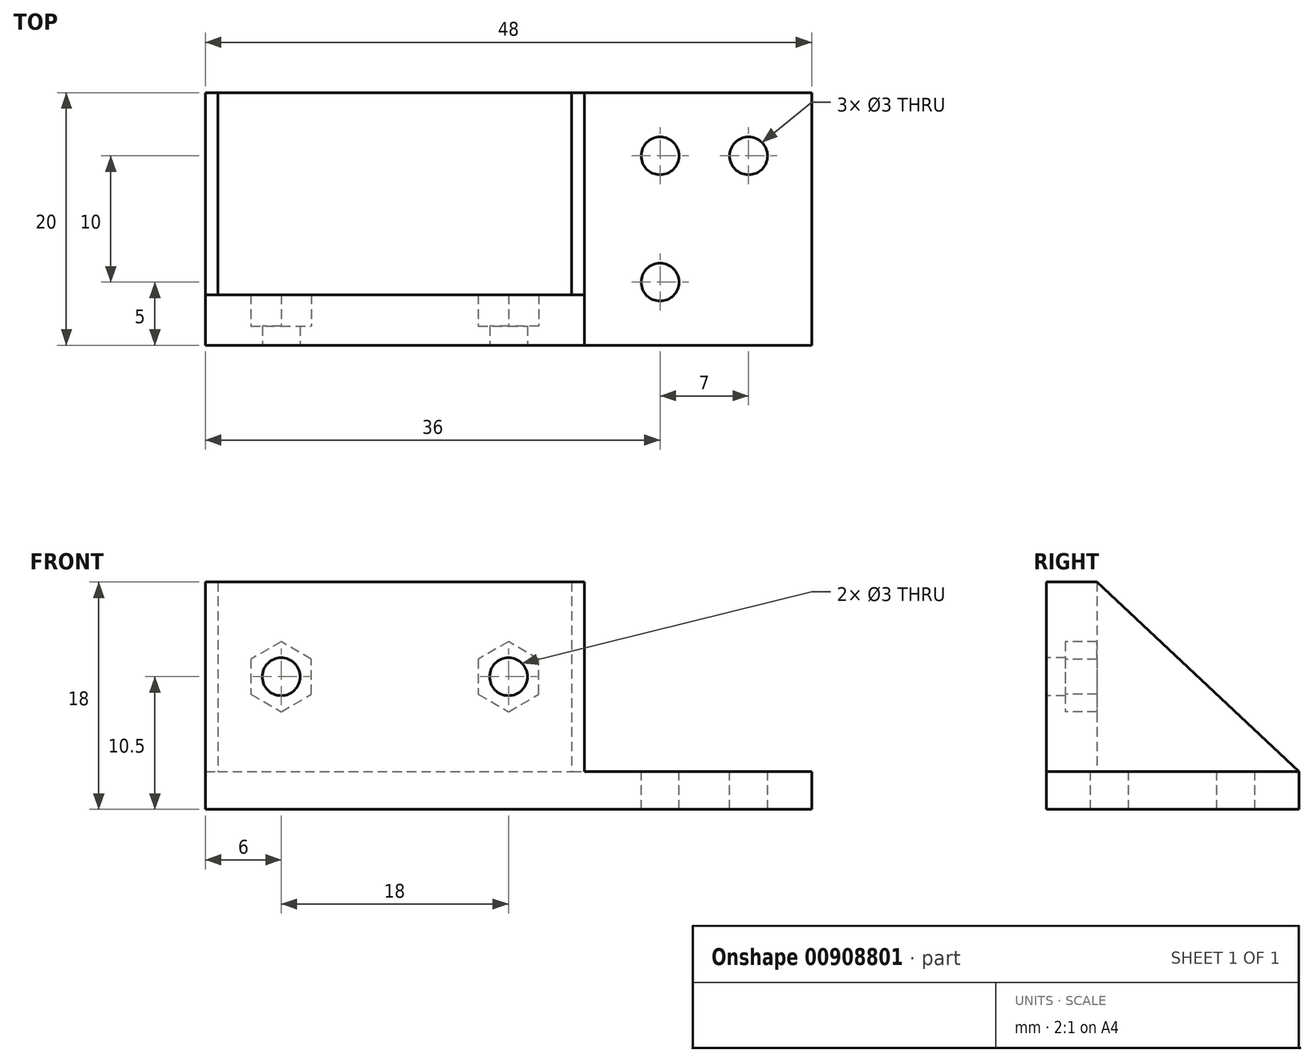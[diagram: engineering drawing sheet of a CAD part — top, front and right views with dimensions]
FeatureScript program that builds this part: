
annotation { "Feature Type Name" : "Feature", "Feature Type Description" : "" }
export const myFeature = defineFeature(function(context is Context, id is Id, definition is map)
    precondition{}
    {
        {
            var Q0;
            Q0=qCreatedBy(makeId("Top.planeOp"),FACE);
            var sketch = newSketch(context, id + "F0", { "sketchPlane" : qUnion([Q0])});
            skLineSegment(sketch, "E0.bottom", {"start": v(-24, 10) * mm, "end": v(24, 10) * mm});
            skLineSegment(sketch, "E0.top", {"start": v(-24, -10) * mm, "end": v(24, -10) * mm});
            skLineSegment(sketch, "E0.left", {"start": v(-24, 10) * mm, "end": v(-24, -10) * mm});
            skLineSegment(sketch, "E0.right", {"start": v(24, 10) * mm, "end": v(24, -10) * mm});
            skSolve(sketch);
        }
        {
            var Q0;
            Q0=makeQuery(id+"F0.imprint","IMPRINT",FACE,{"disambiguationData":[TD([[makeQuery(id+"F0.imprint","IMPRINT",EDGE,{"derivedFrom":sQuery(id+"F0.wireOp",EDGE,"E0.bottom")}),-1.0]])]});
            extrude(context, id + "F1", {"entities" : qUnion([Q0]), "depth" : 3 * mm, "offsetDistance" : 25 * mm});
        }
        {
            var Q0;
            Q0=makeQuery(id+"F1.opExtrude","CAP_FACE",FACE,{"disambiguationData":[OSD([sQuery(id+"F0.wireOp",EDGE,"E0.bottom"),sQuery(id+"F0.wireOp",EDGE,"E0.top"),sQuery(id+"F0.wireOp",EDGE,"E0.left"),sQuery(id+"F0.wireOp",EDGE,"E0.right")])],"isStart":false});
            var sketch = newSketch(context, id + "F2", { "sketchPlane" : qUnion([Q0])});
            skLineSegment(sketch, "E1.bottom", {"start": v(-24, -10) * mm, "end": v(6, -10) * mm});
            skLineSegment(sketch, "E1.top", {"start": v(-24, -8.5) * mm, "end": v(6, -8.5) * mm});
            skLineSegment(sketch, "E1.left", {"start": v(-24, -10) * mm, "end": v(-24, -8.5) * mm});
            skLineSegment(sketch, "E1.right", {"start": v(6, -10) * mm, "end": v(6, -8.5) * mm});
            skSolve(sketch);
        }
        {
            var Q0;
            Q0 = qSketchRegion(id + "F2", true);
            extrude(context, id + "F3", {"entities" : qUnion([Q0]), "operationType" : NewBodyOperationType.ADD, "depth" : 15 * mm, "offsetDistance" : 25 * mm});
        }
        {
            var Q0;
            Q0=makeQuery(id+"F3.boolean.opBoolean","MERGE",FACE,{"derivedFrom":[makeQuery(id+"F1.opExtrude","SWEPT_FACE",FACE,{"disambiguationData":[OSD([sQuery(id+"F0.wireOp",EDGE,"E0.top")])]}),makeQuery(id+"F3.opExtrude","SWEPT_FACE",FACE,{"disambiguationData":[OSD([sQuery(id+"F2.wireOp",EDGE,"E1.bottom")])]})]});
            var sketch = newSketch(context, id + "F4", { "sketchPlane" : qUnion([Q0])});
            skPoint(sketch, "E2", {"position": v(-18, 10.5) * mm});
            skPoint(sketch, "E3", {"position": v(0, 10.5) * mm});
            skLineSegment(sketch, "E4", {"start": v(-9, 16.14) * mm, "end": v(-9, 2.45) * mm, "construction": true});
            skLineSegment(sketch, "E5", {"start": v(6, 3) * mm, "end": v(-24, 3) * mm, "construction": true});
            skLineSegment(sketch, "E6", {"start": v(-18, 3) * mm, "end": v(-18, 18) * mm, "construction": true});
            skSolve(sketch);
        }
        {
            var Q0;
            Q0=makeQuery(id+"F1.opExtrude","CAP_FACE",FACE,{"disambiguationData":[OSD([sQuery(id+"F0.wireOp",EDGE,"E0.bottom"),sQuery(id+"F0.wireOp",EDGE,"E0.top"),sQuery(id+"F0.wireOp",EDGE,"E0.left"),sQuery(id+"F0.wireOp",EDGE,"E0.right")])],"isStart":false});
            var sketch = newSketch(context, id + "F5", { "sketchPlane" : qUnion([Q0])});
            skLineSegment(sketch, "E7", {"start": v(12, -20) * mm, "end": v(12, 10) * mm, "construction": true});
            skPoint(sketch, "E8", {"position": v(12, 5) * mm});
            skPoint(sketch, "E9", {"position": v(12, -5) * mm});
            skPoint(sketch, "E10", {"position": v(19, 5) * mm});
            skSolve(sketch);
        }
        {
            var Q0;
            Q0=sQuery(id+"F4.wireOp",VERTEX,"E3");
            var Q1;
            Q1=sQuery(id+"F4.wireOp",VERTEX,"E2");
            var Q2;
            Q2=sQuery(id+"F5.wireOp",VERTEX,"E10");
            var Q3;
            Q3=sQuery(id+"F5.wireOp",VERTEX,"E8");
            var Q4;
            Q4=sQuery(id+"F5.wireOp",VERTEX,"E9");
            var Q5;
            Q5=makeQuery(id+"F1.opExtrude","SWEPT_BODY",BODY,{"disambiguationData":[OSD([sQuery(id+"F0.wireOp",EDGE,"E0.bottom"),sQuery(id+"F0.wireOp",EDGE,"E0.top"),sQuery(id+"F0.wireOp",EDGE,"E0.left"),sQuery(id+"F0.wireOp",EDGE,"E0.right")])]});
            hole(context, id + "F6", {"style" : HoleStyle.SIMPLE, "endStyle" : HoleEndStyle.THROUGH, "holeDiameter" : 3 * mm, "majorDiameter" : 5 * mm, "isTappedThrough" : true, "tappedDepth" : 12 * mm, "tapClearance" : 3, "locations" : qUnion([Q0, Q1, Q2, Q3, Q4]), "scope" : qUnion([Q5])});
        }
        {
            var Q0;
            Q0=makeQuery(id+"F3.opExtrude","SWEPT_FACE",FACE,{"disambiguationData":[OSD([sQuery(id+"F2.wireOp",EDGE,"E1.top")])]});
            var sketch = newSketch(context, id + "F7", { "sketchPlane" : qUnion([Q0])});
            skCircle(sketch, "E11.cCircle", {"center": v(18, 10.5) * mm, "radius": 2.4 * mm, "construction": true});
            skLineSegment(sketch, "E11.0", {"start": v(18, 7.73) * mm, "end": v(15.6, 9.11) * mm});
            skLineSegment(sketch, "E11.1", {"start": v(15.6, 9.11) * mm, "end": v(15.6, 11.89) * mm});
            skLineSegment(sketch, "E11.2", {"start": v(15.6, 11.89) * mm, "end": v(18, 13.27) * mm});
            skLineSegment(sketch, "E11.3", {"start": v(18, 13.27) * mm, "end": v(20.4, 11.89) * mm});
            skLineSegment(sketch, "E11.4", {"start": v(20.4, 11.89) * mm, "end": v(20.4, 9.11) * mm});
            skLineSegment(sketch, "E11.5", {"start": v(20.4, 9.11) * mm, "end": v(18, 7.73) * mm});
            skPoint(sketch, "E11.0.midPoint", {"position": v(16.8, 8.42) * mm});
            skCircle(sketch, "E12.cCircle", {"center": v(0, 10.5) * mm, "radius": 2.4 * mm, "construction": true});
            skLineSegment(sketch, "E12.0", {"start": v(2.4, 9.11) * mm, "end": v(0, 7.73) * mm});
            skLineSegment(sketch, "E12.1", {"start": v(0, 7.73) * mm, "end": v(-2.4, 9.11) * mm});
            skLineSegment(sketch, "E12.2", {"start": v(-2.4, 9.11) * mm, "end": v(-2.4, 11.89) * mm});
            skLineSegment(sketch, "E12.3", {"start": v(-2.4, 11.89) * mm, "end": v(0, 13.27) * mm});
            skLineSegment(sketch, "E12.4", {"start": v(0, 13.27) * mm, "end": v(2.4, 11.89) * mm});
            skLineSegment(sketch, "E12.5", {"start": v(2.4, 11.89) * mm, "end": v(2.4, 9.11) * mm});
            skPoint(sketch, "E12.0.midPoint", {"position": v(1.2, 8.42) * mm});
            skSolve(sketch);
        }
        {
            var Q0;
            Q0=makeQuery(id+"F7.imprint","IMPRINT",FACE,{"disambiguationData":[TD([[makeQuery(id+"F7.imprint","IMPRINT",EDGE,{"derivedFrom":sQuery(id+"F7.wireOp",EDGE,"E11.0")}),1.0]])]});
            extrude(context, id + "F8", {"entities" : qUnion([Q0]), "operationType" : NewBodyOperationType.ADD, "depth" : 2.5 * mm, "offsetDistance" : 25 * mm});
        }
        {
            var Q0;
            Q0=makeQuery(id+"F3.boolean.opBoolean","MERGE",FACE,{"derivedFrom":[makeQuery(id+"F1.opExtrude","SWEPT_FACE",FACE,{"disambiguationData":[OSD([sQuery(id+"F0.wireOp",EDGE,"E0.left")])]}),makeQuery(id+"F3.opExtrude","SWEPT_FACE",FACE,{"disambiguationData":[OSD([sQuery(id+"F2.wireOp",EDGE,"E1.left")])]})]});
            var sketch = newSketch(context, id + "F9", { "sketchPlane" : qUnion([Q0])});
            skLineSegment(sketch, "E13", {"start": v(-10, 3) * mm, "end": v(6, 18) * mm});
            skSolve(sketch);
        }
        {
            var Q0;
            Q0=makeQuery(id+"F3.opExtrude","SWEPT_FACE",FACE,{"disambiguationData":[OSD([sQuery(id+"F2.wireOp",EDGE,"E1.right")])]});
            var sketch = newSketch(context, id + "F10", { "sketchPlane" : qUnion([Q0])});
            skLineSegment(sketch, "E14", {"start": v(-6, 18) * mm, "end": v(10, 3) * mm});
            skLineSegment(sketch, "E15", {"start": v(10, 3) * mm, "end": v(-6, 3) * mm});
            skSolve(sketch);
        }
        {
            var Q0;
            {var subQ0=sQuery(id+"F9.wireOp",EDGE,"E13");Q0=makeQuery(id+"F9.imprint","IMPRINT",FACE,{"disambiguationData":[TD([[makeQuery(id+"F9.imprint","IMPRINT",EDGE,{"derivedFrom":subQ0}),-1.0]])]});}
            extrude(context, id + "F11", {"entities" : qUnion([Q0]), "operationType" : NewBodyOperationType.ADD, "oppositeDirection" : true, "depth" : 1 * mm, "offsetDistance" : 25 * mm});
        }
        {
            var Q0;
            Q0=makeQuery(id+"F10.imprint","IMPRINT",FACE,{"disambiguationData":[TD([[makeQuery(id+"F10.imprint","IMPRINT",EDGE,{"derivedFrom":sQuery(id+"F10.wireOp",EDGE,"E14")}),-1.0]])]});
            extrude(context, id + "F12", {"entities" : qUnion([Q0]), "operationType" : NewBodyOperationType.ADD, "oppositeDirection" : true, "depth" : 1 * mm, "offsetDistance" : 25 * mm});
        }
    });
